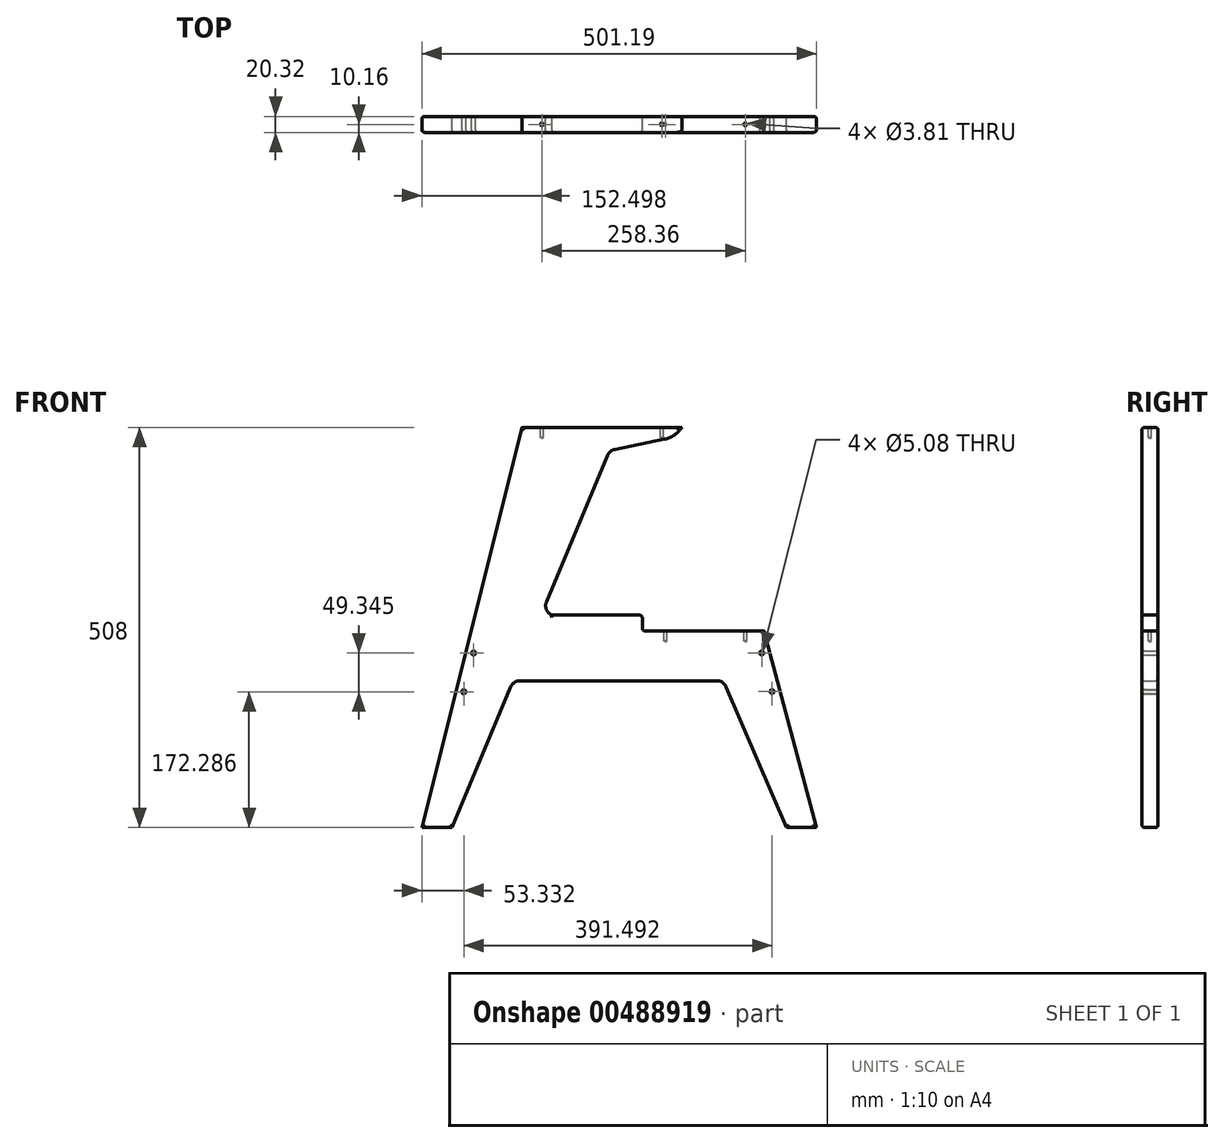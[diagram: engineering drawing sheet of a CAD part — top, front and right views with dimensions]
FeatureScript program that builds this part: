
annotation { "Feature Type Name" : "Feature", "Feature Type Description" : "" }
export const myFeature = defineFeature(function(context is Context, id is Id, definition is map)
    precondition{}
    {
        {
            var Q0;
            Q0=qCreatedBy(makeId("Front.planeOp"),FACE);
            var sketch = newSketch(context, id + "F0", { "sketchPlane" : qUnion([Q0])});
            skLineSegment(sketch, "E0.top", {"start": v(-323.4, -294.33) * mm, "end": v(-285.3, -294.33) * mm});
            skLineSegment(sketch, "E1", {"start": v(-285.3, -294.33) * mm, "end": v(-210.53, -115.74) * mm});
            skLineSegment(sketch, "E2", {"start": v(177.8, -294.33) * mm, "end": v(139.7, -294.33) * mm});
            skLineSegment(sketch, "E3", {"start": v(139.7, -294.33) * mm, "end": v(63.15, -115.64) * mm});
            skLineSegment(sketch, "E4", {"start": v(59.85, -107.94) * mm, "end": v(59.95, -107.94) * mm});
            skLineSegment(sketch, "E5", {"start": v(-198.82, -107.94) * mm, "end": v(51.47, -107.94) * mm});
            skLineSegment(sketch, "E6", {"start": v(59.85, -107.94) * mm, "end": v(59.85, -107.94) * mm});
            skLineSegment(sketch, "E7", {"start": v(-285.3, -294.33) * mm, "end": v(-285.3, -294.33) * mm});
            skLineSegment(sketch, "E8", {"start": v(139.7, -294.33) * mm, "end": v(177.8, -294.33) * mm});
            skLineSegment(sketch, "E9", {"start": v(139.7, -294.33) * mm, "end": v(139.7, -294.33) * mm});
            skLineSegment(sketch, "E10", {"start": v(-165.21, -7.76) * mm, "end": v(-87.28, 178.4) * mm});
            skArc(sketch, "E11.filletArc", {"start": v(-165.21, -7.76) * mm, "mid": v(-165.22, -17.55) * mm, "end": v(-158.26, -24.44) * mm});
            skPoint(sketch, "E12.visualSharp", {"position": v(-207.27, -107.94) * mm});
            skArc(sketch, "E12.filletArc", {"start": v(-198.82, -107.94) * mm, "mid": v(-205.85, -110.07) * mm, "end": v(-210.53, -115.74) * mm});
            skPoint(sketch, "E13.visualSharp", {"position": v(59.85, -107.94) * mm});
            skArc(sketch, "E13.filletArc", {"start": v(63.15, -115.64) * mm, "mid": v(58.47, -110.04) * mm, "end": v(51.47, -107.94) * mm});
            skLineSegment(sketch, "E14", {"start": v(-47.15, -24.44) * mm, "end": v(-158.26, -24.44) * mm});
            skLineSegment(sketch, "E15", {"start": v(-39.53, -44.76) * mm, "end": v(111.46, -44.76) * mm});
            skLineSegment(sketch, "E16", {"start": v(-196.4, 213.67) * mm, "end": v(-323.4, -294.33) * mm});
            skLineSegment(sketch, "E17", {"start": v(-196.4, 213.67) * mm, "end": v(6.8, 213.67) * mm});
            skLineSegment(sketch, "E18", {"start": v(111.46, -44.76) * mm, "end": v(177.8, -294.33) * mm});
            skLineSegment(sketch, "E19", {"start": v(-78.13, 185.94) * mm, "end": v(-14.9, 199) * mm});
            skArc(sketch, "E20", {"start": v(-14.9, 199) * mm, "mid": v(-2.6, 204.18) * mm, "end": v(6.8, 213.67) * mm});
            skPoint(sketch, "E21.visualSharp", {"position": v(-84.7, 184.58) * mm});
            skArc(sketch, "E21.filletArc", {"start": v(-78.13, 185.94) * mm, "mid": v(-83.64, 183.3) * mm, "end": v(-87.28, 178.4) * mm});
            skCircle(sketch, "E22", {"center": v(-257.61, -72.8) * mm, "radius": 2.54 * mm});
            skCircle(sketch, "E23", {"center": v(-270.06, -122.04) * mm, "radius": 2.54 * mm});
            skCircle(sketch, "E24", {"center": v(108.38, -72.7) * mm, "radius": 2.54 * mm});
            skCircle(sketch, "E25", {"center": v(121.43, -121.8) * mm, "radius": 2.54 * mm});
            skLineSegment(sketch, "E26", {"start": v(-43.34, -40.95) * mm, "end": v(-43.34, -28.25) * mm});
            skPoint(sketch, "E27.visualSharp", {"position": v(-43.34, -44.76) * mm});
            skArc(sketch, "E27.filletArc", {"start": v(-43.34, -40.95) * mm, "mid": v(-42.23, -43.64) * mm, "end": v(-39.53, -44.76) * mm});
            skPoint(sketch, "E28.visualSharp", {"position": v(-43.34, -24.44) * mm});
            skArc(sketch, "E28.filletArc", {"start": v(-43.34, -28.25) * mm, "mid": v(-44.46, -25.56) * mm, "end": v(-47.15, -24.44) * mm});
            skSolve(sketch);
        }
        {
            var Q0;
            Q0=makeQuery(id+"F0.imprint","IMPRINT",FACE,{"disambiguationData":[TD([[makeQuery(id+"F0.imprint","IMPRINT",EDGE,{"derivedFrom":sQuery(id+"F0.wireOp",EDGE,"E0.top")}),1.0]])]});
            extrude(context, id + "F1", {"entities" : qUnion([Q0]), "endBound" : BoundingType.SYMMETRIC, "depth" : 20.32 * mm});
        }
        {
            var Q0;
            Q0=makeQuery(id+"F1.opExtrude","CAP_FACE",FACE,{"disambiguationData":[OSD([sQuery(id+"F0.wireOp",EDGE,"E0.top"),sQuery(id+"F0.wireOp",EDGE,"E1"),sQuery(id+"F0.wireOp",EDGE,"E3"),sQuery(id+"F0.wireOp",EDGE,"E5"),sQuery(id+"F0.wireOp",EDGE,"E8"),sQuery(id+"F0.wireOp",EDGE,"E10"),sQuery(id+"F0.wireOp",EDGE,"E11.filletArc"),sQuery(id+"F0.wireOp",EDGE,"E12.filletArc"),sQuery(id+"F0.wireOp",EDGE,"E13.filletArc"),sQuery(id+"F0.wireOp",EDGE,"E14"),sQuery(id+"F0.wireOp",EDGE,"E15"),sQuery(id+"F0.wireOp",EDGE,"E16"),sQuery(id+"F0.wireOp",EDGE,"E17"),sQuery(id+"F0.wireOp",EDGE,"E18"),sQuery(id+"F0.wireOp",EDGE,"E19"),sQuery(id+"F0.wireOp",EDGE,"E20"),sQuery(id+"F0.wireOp",EDGE,"E21.filletArc"),sQuery(id+"F0.wireOp",EDGE,"E22"),sQuery(id+"F0.wireOp",EDGE,"E23"),sQuery(id+"F0.wireOp",EDGE,"E24"),sQuery(id+"F0.wireOp",EDGE,"E25"),sQuery(id+"F0.wireOp",EDGE,"E26"),sQuery(id+"F0.wireOp",EDGE,"E27.filletArc"),sQuery(id+"F0.wireOp",EDGE,"E28.filletArc")])],"isStart":false});
            var Q1;
            Q1=makeQuery(id+"F1.opExtrude","CAP_FACE",FACE,{"disambiguationData":[OSD([sQuery(id+"F0.wireOp",EDGE,"E0.top"),sQuery(id+"F0.wireOp",EDGE,"E1"),sQuery(id+"F0.wireOp",EDGE,"E3"),sQuery(id+"F0.wireOp",EDGE,"E5"),sQuery(id+"F0.wireOp",EDGE,"E8"),sQuery(id+"F0.wireOp",EDGE,"E10"),sQuery(id+"F0.wireOp",EDGE,"E11.filletArc"),sQuery(id+"F0.wireOp",EDGE,"E12.filletArc"),sQuery(id+"F0.wireOp",EDGE,"E13.filletArc"),sQuery(id+"F0.wireOp",EDGE,"E14"),sQuery(id+"F0.wireOp",EDGE,"E15"),sQuery(id+"F0.wireOp",EDGE,"E16"),sQuery(id+"F0.wireOp",EDGE,"E17"),sQuery(id+"F0.wireOp",EDGE,"E18"),sQuery(id+"F0.wireOp",EDGE,"E19"),sQuery(id+"F0.wireOp",EDGE,"E20"),sQuery(id+"F0.wireOp",EDGE,"E21.filletArc"),sQuery(id+"F0.wireOp",EDGE,"E22"),sQuery(id+"F0.wireOp",EDGE,"E23"),sQuery(id+"F0.wireOp",EDGE,"E24"),sQuery(id+"F0.wireOp",EDGE,"E25"),sQuery(id+"F0.wireOp",EDGE,"E26"),sQuery(id+"F0.wireOp",EDGE,"E27.filletArc"),sQuery(id+"F0.wireOp",EDGE,"E28.filletArc")])],"isStart":true});
            fillet(context, id + "F2", {"entities" : qUnion([Q0, Q1]), "radius" : 3.05 * mm, "tangentPropagation" : true, "allowEdgeOverflow" : false});
        }
        {
            var Q0;
            Q0=makeQuery(id+"F1.opExtrude","SWEPT_FACE",FACE,{"disambiguationData":[OSD([sQuery(id+"F0.wireOp",EDGE,"E17")])]});
            var sketch = newSketch(context, id + "F3", { "sketchPlane" : qUnion([Q0])});
            skLineSegment(sketch, "E29", {"start": v(-170.9, 0) * mm, "end": v(-18.5, 0) * mm});
            skSolve(sketch);
        }
        {
            var Q0;
            Q0=sQuery(id+"F3.wireOp",VERTEX,"E29.start");
            var Q1;
            Q1=makeQuery(id+"F1.opExtrude","SWEPT_BODY",BODY,{"disambiguationData":[OSD([sQuery(id+"F0.wireOp",EDGE,"E0.top"),sQuery(id+"F0.wireOp",EDGE,"E1"),sQuery(id+"F0.wireOp",EDGE,"E3"),sQuery(id+"F0.wireOp",EDGE,"E5"),sQuery(id+"F0.wireOp",EDGE,"E8"),sQuery(id+"F0.wireOp",EDGE,"E10"),sQuery(id+"F0.wireOp",EDGE,"E11.filletArc"),sQuery(id+"F0.wireOp",EDGE,"E12.filletArc"),sQuery(id+"F0.wireOp",EDGE,"E13.filletArc"),sQuery(id+"F0.wireOp",EDGE,"E14"),sQuery(id+"F0.wireOp",EDGE,"E15"),sQuery(id+"F0.wireOp",EDGE,"E16"),sQuery(id+"F0.wireOp",EDGE,"E17"),sQuery(id+"F0.wireOp",EDGE,"E18"),sQuery(id+"F0.wireOp",EDGE,"E19"),sQuery(id+"F0.wireOp",EDGE,"E20"),sQuery(id+"F0.wireOp",EDGE,"E21.filletArc"),sQuery(id+"F0.wireOp",EDGE,"E22"),sQuery(id+"F0.wireOp",EDGE,"E23"),sQuery(id+"F0.wireOp",EDGE,"E24"),sQuery(id+"F0.wireOp",EDGE,"E25"),sQuery(id+"F0.wireOp",EDGE,"E26"),sQuery(id+"F0.wireOp",EDGE,"E27.filletArc"),sQuery(id+"F0.wireOp",EDGE,"E28.filletArc")])]});
            hole(context, id + "F4", {"style" : HoleStyle.SIMPLE, "endStyle" : HoleEndStyle.BLIND, "holeDiameter" : 3.8 * mm, "holeDepth" : 12.7 * mm, "isTappedThrough" : true, "tappedDepth" : 12.7 * mm, "tapClearance" : 3, "locations" : qUnion([Q0]), "scope" : qUnion([Q1])});
        }
        {
            var Q0;
            Q0=sQuery(id+"F3.wireOp",VERTEX,"E29.end");
            var Q1;
            Q1=makeQuery(id+"F1.opExtrude","SWEPT_BODY",BODY,{"disambiguationData":[OSD([sQuery(id+"F0.wireOp",EDGE,"E0.top"),sQuery(id+"F0.wireOp",EDGE,"E1"),sQuery(id+"F0.wireOp",EDGE,"E3"),sQuery(id+"F0.wireOp",EDGE,"E5"),sQuery(id+"F0.wireOp",EDGE,"E8"),sQuery(id+"F0.wireOp",EDGE,"E10"),sQuery(id+"F0.wireOp",EDGE,"E11.filletArc"),sQuery(id+"F0.wireOp",EDGE,"E12.filletArc"),sQuery(id+"F0.wireOp",EDGE,"E13.filletArc"),sQuery(id+"F0.wireOp",EDGE,"E14"),sQuery(id+"F0.wireOp",EDGE,"E15"),sQuery(id+"F0.wireOp",EDGE,"E16"),sQuery(id+"F0.wireOp",EDGE,"E17"),sQuery(id+"F0.wireOp",EDGE,"E18"),sQuery(id+"F0.wireOp",EDGE,"E19"),sQuery(id+"F0.wireOp",EDGE,"E20"),sQuery(id+"F0.wireOp",EDGE,"E21.filletArc"),sQuery(id+"F0.wireOp",EDGE,"E22"),sQuery(id+"F0.wireOp",EDGE,"E23"),sQuery(id+"F0.wireOp",EDGE,"E24"),sQuery(id+"F0.wireOp",EDGE,"E25"),sQuery(id+"F0.wireOp",EDGE,"E26"),sQuery(id+"F0.wireOp",EDGE,"E27.filletArc"),sQuery(id+"F0.wireOp",EDGE,"E28.filletArc")])]});
            hole(context, id + "F5", {"style" : HoleStyle.SIMPLE, "endStyle" : HoleEndStyle.BLIND, "holeDiameter" : 3.8 * mm, "holeDepth" : 12.7 * mm, "isTappedThrough" : true, "tappedDepth" : 12.7 * mm, "tapClearance" : 3, "locations" : qUnion([Q0]), "scope" : qUnion([Q1])});
        }
        {
            var Q0;
            Q0=makeQuery(id+"F1.opExtrude","SWEPT_FACE",FACE,{"disambiguationData":[OSD([sQuery(id+"F0.wireOp",EDGE,"E15")])]});
            var sketch = newSketch(context, id + "F6", { "sketchPlane" : qUnion([Q0])});
            skLineSegment(sketch, "E30", {"start": v(87.47, 0) * mm, "end": v(-14.13, 0) * mm});
            skLineSegment(sketch, "E31", {"start": v(-14.13, 0) * mm, "end": v(-39.53, 0) * mm});
            skSolve(sketch);
        }
        {
            var Q0;
            Q0=sQuery(id+"F6.wireOp",VERTEX,"E31.start");
            var Q1;
            Q1=makeQuery(id+"F1.opExtrude","SWEPT_BODY",BODY,{"disambiguationData":[OSD([sQuery(id+"F0.wireOp",EDGE,"E0.top"),sQuery(id+"F0.wireOp",EDGE,"E1"),sQuery(id+"F0.wireOp",EDGE,"E3"),sQuery(id+"F0.wireOp",EDGE,"E5"),sQuery(id+"F0.wireOp",EDGE,"E8"),sQuery(id+"F0.wireOp",EDGE,"E10"),sQuery(id+"F0.wireOp",EDGE,"E11.filletArc"),sQuery(id+"F0.wireOp",EDGE,"E12.filletArc"),sQuery(id+"F0.wireOp",EDGE,"E13.filletArc"),sQuery(id+"F0.wireOp",EDGE,"E14"),sQuery(id+"F0.wireOp",EDGE,"E15"),sQuery(id+"F0.wireOp",EDGE,"E16"),sQuery(id+"F0.wireOp",EDGE,"E17"),sQuery(id+"F0.wireOp",EDGE,"E18"),sQuery(id+"F0.wireOp",EDGE,"E19"),sQuery(id+"F0.wireOp",EDGE,"E20"),sQuery(id+"F0.wireOp",EDGE,"E21.filletArc"),sQuery(id+"F0.wireOp",EDGE,"E22"),sQuery(id+"F0.wireOp",EDGE,"E23"),sQuery(id+"F0.wireOp",EDGE,"E24"),sQuery(id+"F0.wireOp",EDGE,"E25"),sQuery(id+"F0.wireOp",EDGE,"E26"),sQuery(id+"F0.wireOp",EDGE,"E27.filletArc"),sQuery(id+"F0.wireOp",EDGE,"E28.filletArc")])]});
            hole(context, id + "F7", {"style" : HoleStyle.SIMPLE, "endStyle" : HoleEndStyle.BLIND, "holeDiameter" : 3.8 * mm, "holeDepth" : 12.7 * mm, "isTappedThrough" : true, "tappedDepth" : 12.7 * mm, "tapClearance" : 3, "locations" : qUnion([Q0]), "scope" : qUnion([Q1])});
        }
        {
            var Q0;
            Q0=sQuery(id+"F6.wireOp",VERTEX,"E30.start");
            var Q1;
            Q1=makeQuery(id+"F1.opExtrude","SWEPT_BODY",BODY,{"disambiguationData":[OSD([sQuery(id+"F0.wireOp",EDGE,"E0.top"),sQuery(id+"F0.wireOp",EDGE,"E1"),sQuery(id+"F0.wireOp",EDGE,"E3"),sQuery(id+"F0.wireOp",EDGE,"E5"),sQuery(id+"F0.wireOp",EDGE,"E8"),sQuery(id+"F0.wireOp",EDGE,"E10"),sQuery(id+"F0.wireOp",EDGE,"E11.filletArc"),sQuery(id+"F0.wireOp",EDGE,"E12.filletArc"),sQuery(id+"F0.wireOp",EDGE,"E13.filletArc"),sQuery(id+"F0.wireOp",EDGE,"E14"),sQuery(id+"F0.wireOp",EDGE,"E15"),sQuery(id+"F0.wireOp",EDGE,"E16"),sQuery(id+"F0.wireOp",EDGE,"E17"),sQuery(id+"F0.wireOp",EDGE,"E18"),sQuery(id+"F0.wireOp",EDGE,"E19"),sQuery(id+"F0.wireOp",EDGE,"E20"),sQuery(id+"F0.wireOp",EDGE,"E21.filletArc"),sQuery(id+"F0.wireOp",EDGE,"E22"),sQuery(id+"F0.wireOp",EDGE,"E23"),sQuery(id+"F0.wireOp",EDGE,"E24"),sQuery(id+"F0.wireOp",EDGE,"E25"),sQuery(id+"F0.wireOp",EDGE,"E26"),sQuery(id+"F0.wireOp",EDGE,"E27.filletArc"),sQuery(id+"F0.wireOp",EDGE,"E28.filletArc")])]});
            hole(context, id + "F8", {"style" : HoleStyle.SIMPLE, "endStyle" : HoleEndStyle.BLIND, "holeDiameter" : 3.8 * mm, "holeDepth" : 12.7 * mm, "isTappedThrough" : true, "tappedDepth" : 12.7 * mm, "tapClearance" : 3, "locations" : qUnion([Q0]), "scope" : qUnion([Q1])});
        }
    });
